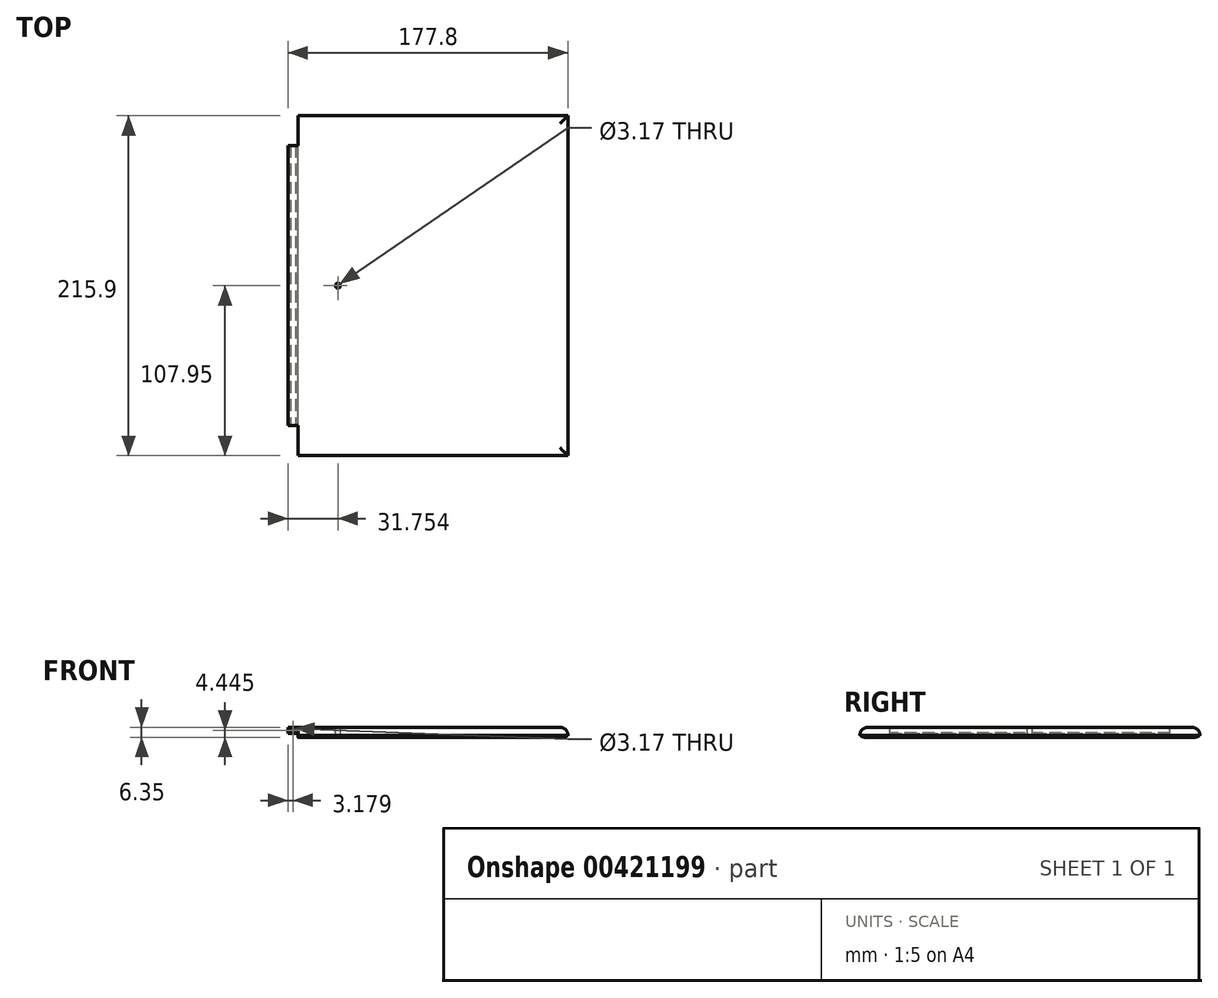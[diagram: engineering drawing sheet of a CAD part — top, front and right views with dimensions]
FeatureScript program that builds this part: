
annotation { "Feature Type Name" : "Feature", "Feature Type Description" : "" }
export const myFeature = defineFeature(function(context is Context, id is Id, definition is map)
    precondition{}
    {
        {
            var Q0;
            Q0=qCreatedBy(makeId("Top.planeOp"),FACE);
            var sketch = newSketch(context, id + "F0", { "sketchPlane" : qUnion([Q0])});
            skLineSegment(sketch, "E0", {"start": v(-11.62, -75.16) * mm, "end": v(-11.62, -94.2) * mm});
            skLineSegment(sketch, "E1", {"start": v(-11.62, -75.16) * mm, "end": v(-11.62, 121.7) * mm});
            skLineSegment(sketch, "E2", {"start": v(-11.62, 121.7) * mm, "end": v(159.83, 121.7) * mm});
            skLineSegment(sketch, "E3", {"start": v(-11.62, -94.2) * mm, "end": v(159.83, -94.2) * mm});
            skLineSegment(sketch, "E4", {"start": v(159.83, -94.2) * mm, "end": v(159.83, 121.7) * mm});
            skPoint(sketch, "E5.endSnap0", {"position": v(159.83, 13.74) * mm});
            skPoint(sketch, "E6.start.orphan", {"position": v(-56.07, 127.68) * mm});
            skPoint(sketch, "E7.start.orphan", {"position": v(-56.07, -75.52) * mm});
            skPoint(sketch, "E8.center.orphan", {"position": v(37.13, 13.74) * mm});
            skPoint(sketch, "E9.orphan", {"position": v(34.59, 13.74) * mm});
            skPoint(sketch, "E10.end.orphan", {"position": v(39.67, 13.74) * mm});
            skLineSegment(sketch, "E11", {"start": v(-11.62, 121.7) * mm, "end": v(-11.62, 102.64) * mm});
            skLineSegment(sketch, "E12", {"start": v(-11.62, -94.2) * mm, "end": v(-11.62, -75.16) * mm});
            skLineSegment(sketch, "E13", {"start": v(-11.62, -75.16) * mm, "end": v(-17.97, -75.16) * mm});
            skLineSegment(sketch, "E14", {"start": v(-17.97, -75.16) * mm, "end": v(-17.97, 102.64) * mm});
            skLineSegment(sketch, "E15", {"start": v(-17.97, 102.64) * mm, "end": v(-11.62, 102.64) * mm});
            skSolve(sketch);
        }
        {
            var Q0;
            Q0=makeQuery(id+"F0.imprint","IMPRINT",FACE,{"disambiguationData":[TD([[makeQuery(id+"F0.imprint","IMPRINT",EDGE,{"derivedFrom":sQuery(id+"F0.wireOp",EDGE,"E1")}),-1.0]])]});
            extrude(context, id + "F1", {"entities" : qUnion([Q0]), "oppositeDirection" : true, "depth" : 6.35 * mm});
        }
        {
            var Q0;
            Q0=makeQuery(id+"F0.imprint","IMPRINT",FACE,{"disambiguationData":[TD([[makeQuery(id+"F0.imprint","IMPRINT",EDGE,{"derivedFrom":sQuery(id+"F0.wireOp",EDGE,"E1")}),1.0]])]});
            extrude(context, id + "F2", {"entities" : qUnion([Q0]), "operationType" : NewBodyOperationType.ADD, "oppositeDirection" : true, "depth" : 3.8 * mm});
        }
        {
            var Q0;
            Q0=makeQuery(id+"F2.opExtrude","SWEPT_FACE",FACE,{"disambiguationData":[OSD([sQuery(id+"F0.wireOp",EDGE,"E13")])]});
            var sketch = newSketch(context, id + "F3", { "sketchPlane" : qUnion([Q0])});
            skCircle(sketch, "E16", {"center": v(-14.8, -1.9) * mm, "radius": 1.59 * mm});
            skPoint(sketch, "E17.trimOffspring.end.orphan", {"position": v(-14.8, -3.81) * mm});
            skPoint(sketch, "E18.start.orphan", {"position": v(-14.8, 0) * mm});
            skSolve(sketch);
        }
        {
            var Q0;
            Q0=makeQuery(id+"F3.imprint","IMPRINT",FACE,{"disambiguationData":[TD([[makeQuery(id+"F3.imprint","IMPRINT",EDGE,{"derivedFrom":sQuery(id+"F3.wireOp",EDGE,"E16")}),1.0]])]});
            extrude(context, id + "F4", {"entities" : qUnion([Q0]), "operationType" : NewBodyOperationType.REMOVE, "oppositeDirection" : true, "depth" : 177.8 * mm});
        }
        {
            var Q0;
            {var subQ0=sQuery(id+"F0.wireOp",EDGE,"E1");Q0=makeQuery(id+"F2.boolean.opBoolean","MERGE",FACE,{"derivedFrom":[makeQuery(id+"F1.opExtrude","CAP_FACE",FACE,{"disambiguationData":[OSD([subQ0,sQuery(id+"F0.wireOp",EDGE,"E2"),sQuery(id+"F0.wireOp",EDGE,"E3"),sQuery(id+"F0.wireOp",EDGE,"E4"),sQuery(id+"F0.wireOp",EDGE,"E11"),sQuery(id+"F0.wireOp",EDGE,"E12")])],"isStart":true}),makeQuery(id+"F2.opExtrude","CAP_FACE",FACE,{"disambiguationData":[OSD([subQ0,sQuery(id+"F0.wireOp",EDGE,"E13"),sQuery(id+"F0.wireOp",EDGE,"E14"),sQuery(id+"F0.wireOp",EDGE,"E15")])],"isStart":true})]});}
            var sketch = newSketch(context, id + "F5", { "sketchPlane" : qUnion([Q0])});
            skCircle(sketch, "E19", {"center": v(13.78, 13.74) * mm, "radius": 1.59 * mm});
            skSolve(sketch);
        }
        {
            var Q0;
            Q0=makeQuery(id+"F5.imprint","IMPRINT",FACE,{"disambiguationData":[TD([[makeQuery(id+"F5.imprint","IMPRINT",EDGE,{"derivedFrom":sQuery(id+"F5.wireOp",EDGE,"E19")}),1.0]])]});
            extrude(context, id + "F6", {"entities" : qUnion([Q0]), "operationType" : NewBodyOperationType.REMOVE, "oppositeDirection" : true, "depth" : 6.35 * mm});
        }
        {
            var Q0;
            Q0=makeQuery(id+"F1.opExtrude","CAP_EDGE",EDGE,{"disambiguationData":[OSD([sQuery(id+"F0.wireOp",EDGE,"E3")])],"isStart":true});
            var Q1;
            Q1=makeQuery(id+"F1.opExtrude","CAP_EDGE",EDGE,{"disambiguationData":[OSD([sQuery(id+"F0.wireOp",EDGE,"E4")])],"isStart":true});
            var Q2;
            Q2=makeQuery(id+"F1.opExtrude","CAP_EDGE",EDGE,{"disambiguationData":[OSD([sQuery(id+"F0.wireOp",EDGE,"E2")])],"isStart":true});
            fillet(context, id + "F7", {"entities" : qUnion([Q0, Q1, Q2]), "radius" : 5.08 * mm, "tangentPropagation" : true, "allowEdgeOverflow" : false});
        }
        {
            var Q0;
            Q0=makeQuery(id+"F1.opExtrude","CAP_EDGE",EDGE,{"disambiguationData":[OSD([sQuery(id+"F0.wireOp",EDGE,"E4")])],"isStart":false});
            var Q1;
            Q1=makeQuery(id+"F1.opExtrude","CAP_EDGE",EDGE,{"disambiguationData":[OSD([sQuery(id+"F0.wireOp",EDGE,"E3")])],"isStart":false});
            var Q2;
            Q2=makeQuery(id+"F1.opExtrude","CAP_EDGE",EDGE,{"disambiguationData":[OSD([sQuery(id+"F0.wireOp",EDGE,"E2")])],"isStart":false});
            fillet(context, id + "F8", {"entities" : qUnion([Q0, Q1, Q2]), "radius" : 5.08 * mm, "tangentPropagation" : true, "allowEdgeOverflow" : false});
        }
    });
